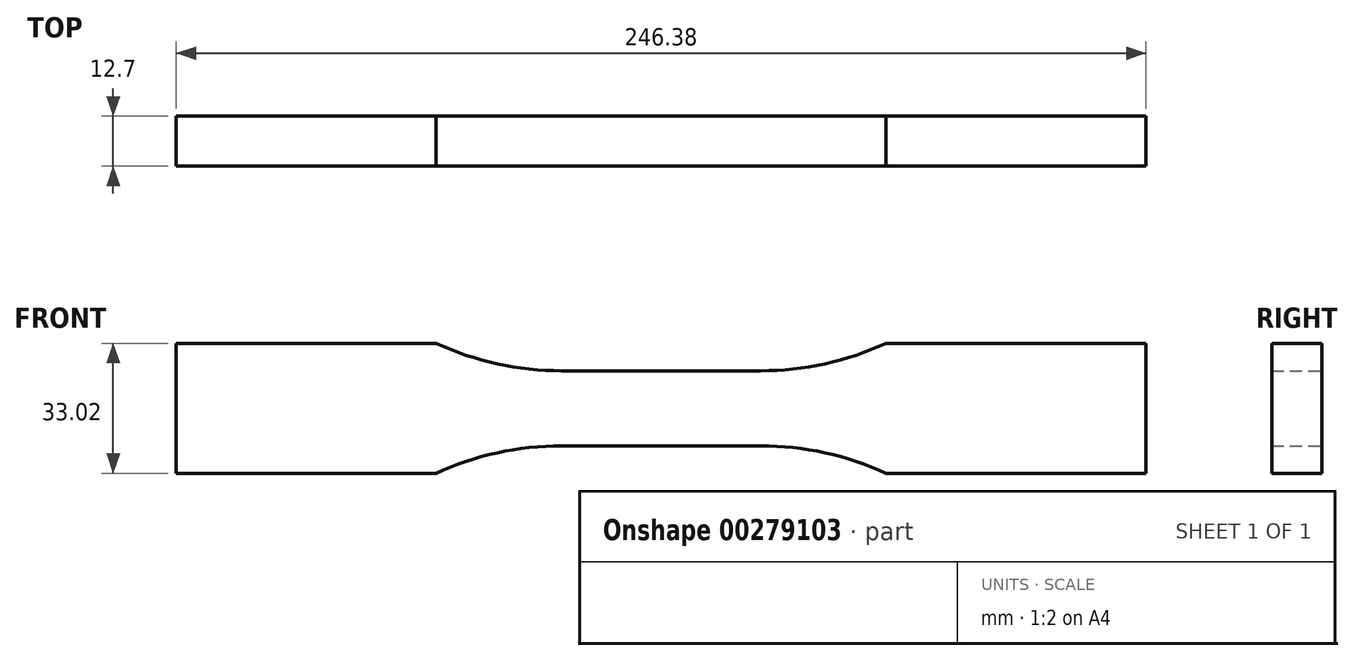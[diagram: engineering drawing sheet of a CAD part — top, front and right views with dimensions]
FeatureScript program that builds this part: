
annotation { "Feature Type Name" : "Feature", "Feature Type Description" : "" }
export const myFeature = defineFeature(function(context is Context, id is Id, definition is map)
    precondition{}
    {
        {
            var Q0;
            Q0=qCreatedBy(makeId("Front.planeOp"),FACE);
            var sketch = newSketch(context, id + "F0", { "sketchPlane" : qUnion([Q0])});
            skLineSegment(sketch, "E0", {"start": v(0, 9.53) * mm, "end": v(25.28, 9.53) * mm});
            skArc(sketch, "E1", {"start": v(25.28, 9.53) * mm, "mid": v(41.6, 11.3) * mm, "end": v(57.15, 16.5) * mm});
            skLineSegment(sketch, "E2", {"start": v(57.15, 16.5) * mm, "end": v(123.2, 16.5) * mm});
            skLineSegment(sketch, "E3", {"start": v(123.2, 16.51) * mm, "end": v(123.2, 0) * mm});
            skLineSegment(sketch, "E4.MirrorCS", {"start": v(0, -9.53) * mm, "end": v(25.28, -9.53) * mm});
            skLineSegment(sketch, "E5.MirrorCS", {"start": v(123.2, -16.51) * mm, "end": v(123.2, 0) * mm});
            skLineSegment(sketch, "E6.MirrorCS", {"start": v(57.15, -16.5) * mm, "end": v(123.2, -16.5) * mm});
            skArc(sketch, "E7.MirrorCS", {"start": v(25.28, -9.53) * mm, "mid": v(41.6, -11.3) * mm, "end": v(57.15, -16.5) * mm});
            skArc(sketch, "E8.MirrorCS", {"start": v(-25.28, -9.53) * mm, "mid": v(-41.6, -11.3) * mm, "end": v(-57.15, -16.5) * mm});
            skLineSegment(sketch, "E9.MirrorCS", {"start": v(-57.15, -16.5) * mm, "end": v(-123.2, -16.51) * mm});
            skLineSegment(sketch, "E10.MirrorCS", {"start": v(0, 9.53) * mm, "end": v(-25.28, 9.53) * mm});
            skArc(sketch, "E11.MirrorCS", {"start": v(-25.28, 9.53) * mm, "mid": v(-41.6, 11.3) * mm, "end": v(-57.15, 16.5) * mm});
            skLineSegment(sketch, "E12.MirrorCS", {"start": v(-57.15, 16.5) * mm, "end": v(-123.2, 16.5) * mm});
            skLineSegment(sketch, "E13.MirrorCS", {"start": v(-123.2, -16.51) * mm, "end": v(-123.2, 0) * mm});
            skLineSegment(sketch, "E14.MirrorCS", {"start": v(-123.2, 16.51) * mm, "end": v(-123.2, 0) * mm});
            skLineSegment(sketch, "E15.MirrorCS", {"start": v(0, -9.52) * mm, "end": v(-25.28, -9.53) * mm});
            skSolve(sketch);
        }
        {
            var Q0;
            Q0 = qSketchRegion(id + "F0", true);
            extrude(context, id + "F1", {"entities" : qUnion([Q0]), "depth" : 12.7 * mm});
        }
    });
